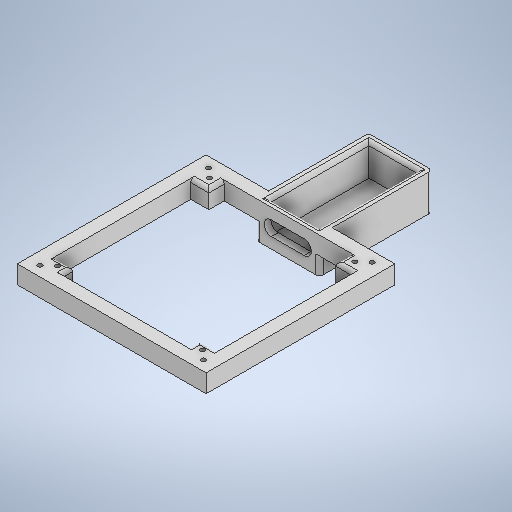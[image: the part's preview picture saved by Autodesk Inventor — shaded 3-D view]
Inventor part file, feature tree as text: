
AUTODESK INVENTOR PART (.ipt)
format: ipt  version: 2025.2 (Build 292293000, 293)  size: 407,040 bytes
history: native  units: in
note: dims shown in document units (in); Inventor stores cm internally (conversion verified against a paired STEP export)
features: extrude x8, thread x8, sketch x8, fillet x1
ambient origin geometry x8: Origin, YZ Plane, XZ Plane, XY Plane, X Axis, Y Axis, Z Axis, Center Point
bodies: Solid1 (feature_tree)
feature tree (25):
  extrude  "Extrusion1"  Depth=5.2in
  extrude  "Extrusion2"  Depth=4.5in
  thread  "Thread1"  [1 undecoded]
  thread  "Thread2"  [1 undecoded]
  thread  "Thread3"  [1 undecoded]
  thread  "Thread4"  [1 undecoded]
  extrude  "Extrusion3"  Depth=4.5in
  thread  "Thread5"  [1 undecoded]
  thread  "Thread6"  [1 undecoded]
  thread  "Thread7"  [1 undecoded]
  thread  "Thread8"  [1 undecoded]
  extrude  "Extrusion4"  Depth=0.12in
  extrude  "Extrusion5"  Depth=1.0in TaperAngle=0.0deg
  extrude  "Extrusion6"  Depth=0.5in TaperAngle=0.0deg
  extrude  "Extrusion8"  Depth=0.5in TaperAngle=0.0deg
  fillet  "Fillet3"  Radius=0.12in
  extrude  "Extrusion9"  Depth=0.875in
  sketch  "Sketch1"  dims[d0=5.2in d1=5.2in]
  sketch  "Sketch2"  dims[d2=2.6in d3=2.6in d4=0.5in d5=0.0in d7=4.65in d8=4.5in d9=0.0in]
  sketch  "Sketch3"  dims[d10=4.65in d11=4.5in d12=0.35in d14=0.35in d15=0.275in d16=0.12in]
  sketch  "Sketch4"  dims[d17=0.12in d18=0.12in]
  sketch  "Sketch5"  dims[d19=0.12in d20=1.0in d21=0.0in]
  sketch  "Sketch6"  dims[d22=0.5in d23=0.0in d24=0.5in d25=0.0in]
  sketch  "Sketch8"  dims[d26=0.5in d27=0.0in d28=0.5in d29=0.0in d30=0.12in]
  sketch  "Sketch9"  dims[d31=0.12in d32=0.12in d33=0.12in d34=4.0in d35=4.0in d36=4.2in d37=4.2in d38=0.0in d39=0.0in d40=0.6in d41=0.5in d42=1.0in d43=0.0in d44=0.5in d45=0.0in d46=0.5in d47=0.0in d48=0.5in d49=0.0in d50=0.5in d51=0.0in d52=4.5in d53=3.75in d54=2.25in d55=3.5in d56=4.5in d57=0.35in d58=1.0in d59=0.0in d60=1.75in d61=1.725in d62=2.75in d63=0.0in d64=1.75in d65=1.0in d66=0.0in d74=1.35in d75=2.725in d76=0.2in d77=0.1875in d78=0.875in d79=0.0in d80=0.1in d81=0.4in d82=0.0in d83=0.45in d84=0.875in d85=0.0in]
note: 8 required parameter values undecoded (feature->parameter linkage not recoverable at this tier; creation-order binding heuristic only, values carry confidence <= 0.55)
